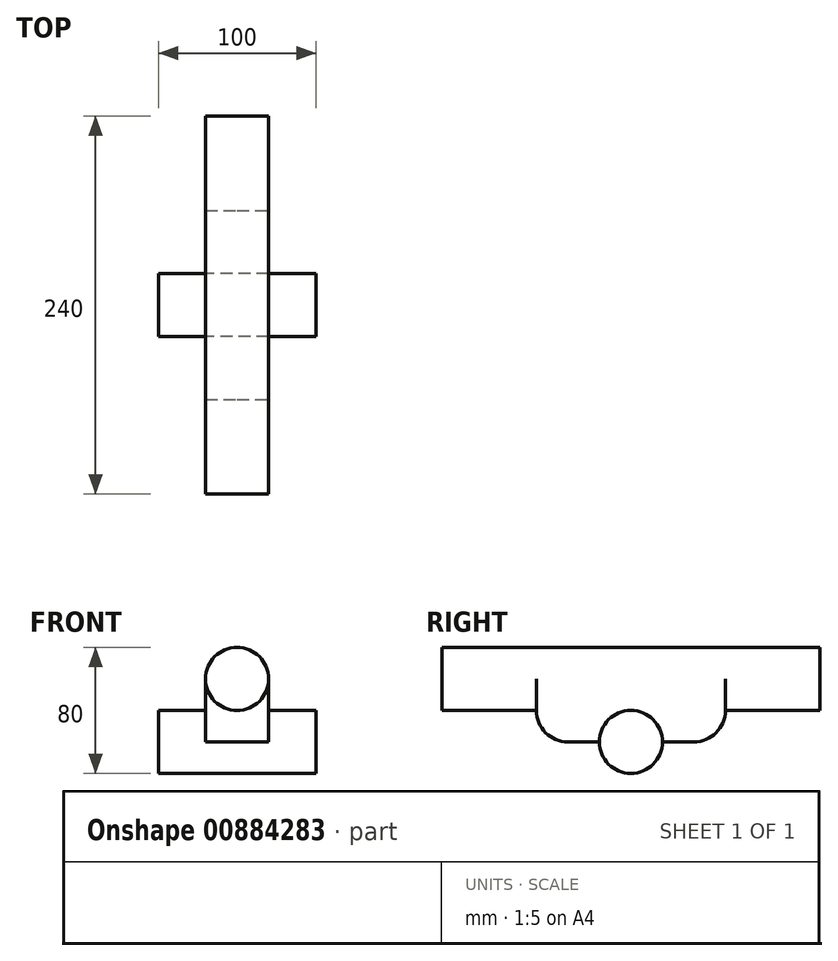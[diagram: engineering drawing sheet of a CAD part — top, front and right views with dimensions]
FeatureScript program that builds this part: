
annotation { "Feature Type Name" : "Feature", "Feature Type Description" : "" }
export const myFeature = defineFeature(function(context is Context, id is Id, definition is map)
    precondition{}
    {
        {
            var Q0;
            Q0=qCreatedBy(makeId("Right.planeOp"),FACE);
            var sketch = newSketch(context, id + "F0", { "sketchPlane" : qUnion([Q0])});
            skLineSegment(sketch, "E0.bottom", {"start": v(-120, 0) * mm, "end": v(120, 0) * mm});
            skLineSegment(sketch, "E0.top", {"start": v(-120, 20) * mm, "end": v(120, 20) * mm});
            skLineSegment(sketch, "E0.left", {"start": v(-120, 0) * mm, "end": v(-120, 20) * mm});
            skLineSegment(sketch, "E0.right", {"start": v(120, 0) * mm, "end": v(120, 20) * mm});
            skLineSegment(sketch, "E1", {"start": v(0, 0) * mm, "end": v(0, 99.29) * mm, "construction": true});
            skLineSegment(sketch, "E2", {"start": v(0, 0) * mm, "end": v(-149.38, 0) * mm, "construction": true});
            skSolve(sketch);
        }
        {
            var Q0;
            Q0=makeQuery(id+"F0.imprint","IMPRINT",FACE,{"disambiguationData":[TD([[makeQuery(id+"F0.imprint","IMPRINT",EDGE,{"derivedFrom":sQuery(id+"F0.wireOp",EDGE,"E0.bottom")}),1.0]])]});
            var Q1;
            Q1=sQuery(id+"F0.wireOp",EDGE,"E0.bottom");
            revolve(context, id + "F1", {"surfaceOperationType" : NewSurfaceOperationType.NEW, "entities" : qUnion([Q0]), "axis" : qUnion([Q1]), "revolveType" : RevolveType.FULL});
        }
        {
            var Q0;
            Q0=qCreatedBy(makeId("Top.planeOp"),FACE);
            var sketch = newSketch(context, id + "F2", { "sketchPlane" : qUnion([Q0])});
            skLineSegment(sketch, "E3.bottom", {"start": v(-20, -60) * mm, "end": v(20, -60) * mm});
            skLineSegment(sketch, "E3.top", {"start": v(-20, 60) * mm, "end": v(20, 60) * mm});
            skLineSegment(sketch, "E3.left", {"start": v(-20, -60) * mm, "end": v(-20, 60) * mm});
            skLineSegment(sketch, "E3.right", {"start": v(20, -60) * mm, "end": v(20, 60) * mm});
            skLineSegment(sketch, "E4", {"start": v(0, 0) * mm, "end": v(-50.08, 0) * mm, "construction": true});
            skLineSegment(sketch, "E5", {"start": v(0, 0) * mm, "end": v(0, 31.03) * mm, "construction": true});
            skSolve(sketch);
        }
        {
            var Q0;
            Q0 = qSketchRegion(id + "F2", true);
            extrude(context, id + "F3", {"entities" : qUnion([Q0]), "operationType" : NewBodyOperationType.ADD, "oppositeDirection" : true, "depth" : 40 * mm, "offsetDistance" : 25 * mm});
        }
        {
            var Q0;
            Q0=makeQuery(id+"F3.opExtrude","CAP_EDGE",EDGE,{"disambiguationData":[OSD([sQuery(id+"F2.wireOp",EDGE,"E3.bottom")])],"isStart":false});
            var Q1;
            Q1=makeQuery(id+"F3.opExtrude","CAP_EDGE",EDGE,{"disambiguationData":[OSD([sQuery(id+"F2.wireOp",EDGE,"E3.top")])],"isStart":false});
            fillet(context, id + "F4", {"entities" : qUnion([Q0, Q1]), "radius" : 20 * mm, "tangentPropagation" : true, "allowEdgeOverflow" : false});
        }
        {
            var Q0;
            Q0=qCreatedBy(makeId("Front.planeOp"),FACE);
            var sketch = newSketch(context, id + "F5", { "sketchPlane" : qUnion([Q0])});
            skLineSegment(sketch, "E6", {"start": v(-49.85, -40) * mm, "end": v(50.15, -40) * mm});
            skLineSegment(sketch, "E7", {"start": v(-49.85, -40) * mm, "end": v(-49.85, -60) * mm});
            skLineSegment(sketch, "E8", {"start": v(-49.85, -60) * mm, "end": v(50.15, -60) * mm});
            skLineSegment(sketch, "E9", {"start": v(50.15, -60) * mm, "end": v(50.15, -40) * mm});
            skLineSegment(sketch, "E10", {"start": v(0.15, -40) * mm, "end": v(87.73, -40) * mm, "construction": true});
            skSolve(sketch);
        }
        {
            var Q0;
            Q0 = qSketchRegion(id + "F5", true);
            var Q1;
            Q1=sQuery(id+"F5.wireOp",EDGE,"E10");
            revolve(context, id + "F6", {"operationType" : NewBodyOperationType.ADD, "surfaceOperationType" : NewSurfaceOperationType.NEW, "entities" : qUnion([Q0]), "axis" : qUnion([Q1]), "revolveType" : RevolveType.FULL});
        }
    });
